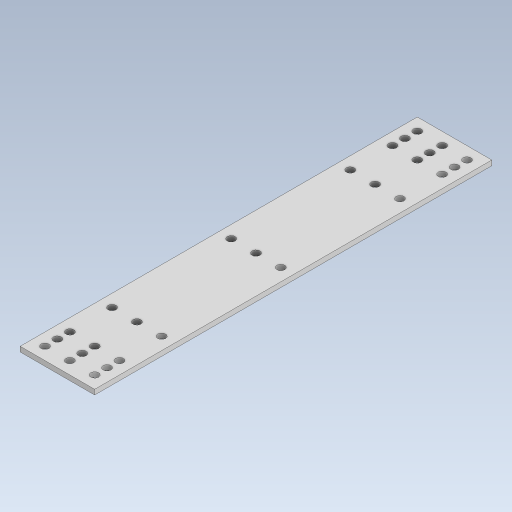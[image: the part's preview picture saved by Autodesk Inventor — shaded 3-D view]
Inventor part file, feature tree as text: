
AUTODESK INVENTOR PART (.ipt)
format: ipt  version: 2023.5 (Build 275446000, 446)  size: 339,968 bytes
history: native  units: mm
features: extrude x1, sketch x1
ambient origin geometry x8: Origin, YZ Plane, XZ Plane, XY Plane, X Axis, Y Axis, Z Axis, Center Point
bodies: Solid1 (feature_tree)
feature tree (2):
  extrude  "Extrusion1"  Depth=80.0mm
  sketch  "Sketch1"  dims[d0=30.0mm d1=80.0mm d2=3.2mm d3=5.0mm d4=5.0mm d5=3.2mm d6=3.2mm d7=3.2mm d8=5.0mm d9=3.2mm d10=3.2mm d11=3.2mm d12=5.0mm d13=3.2mm d14=3.2mm d15=3.2mm d17=3.2mm d18=3.2mm d19=2.0mm d20=0.0mm d21=3.2mm d22=48.0mm d23=3.2mm d24=3.2mm]
